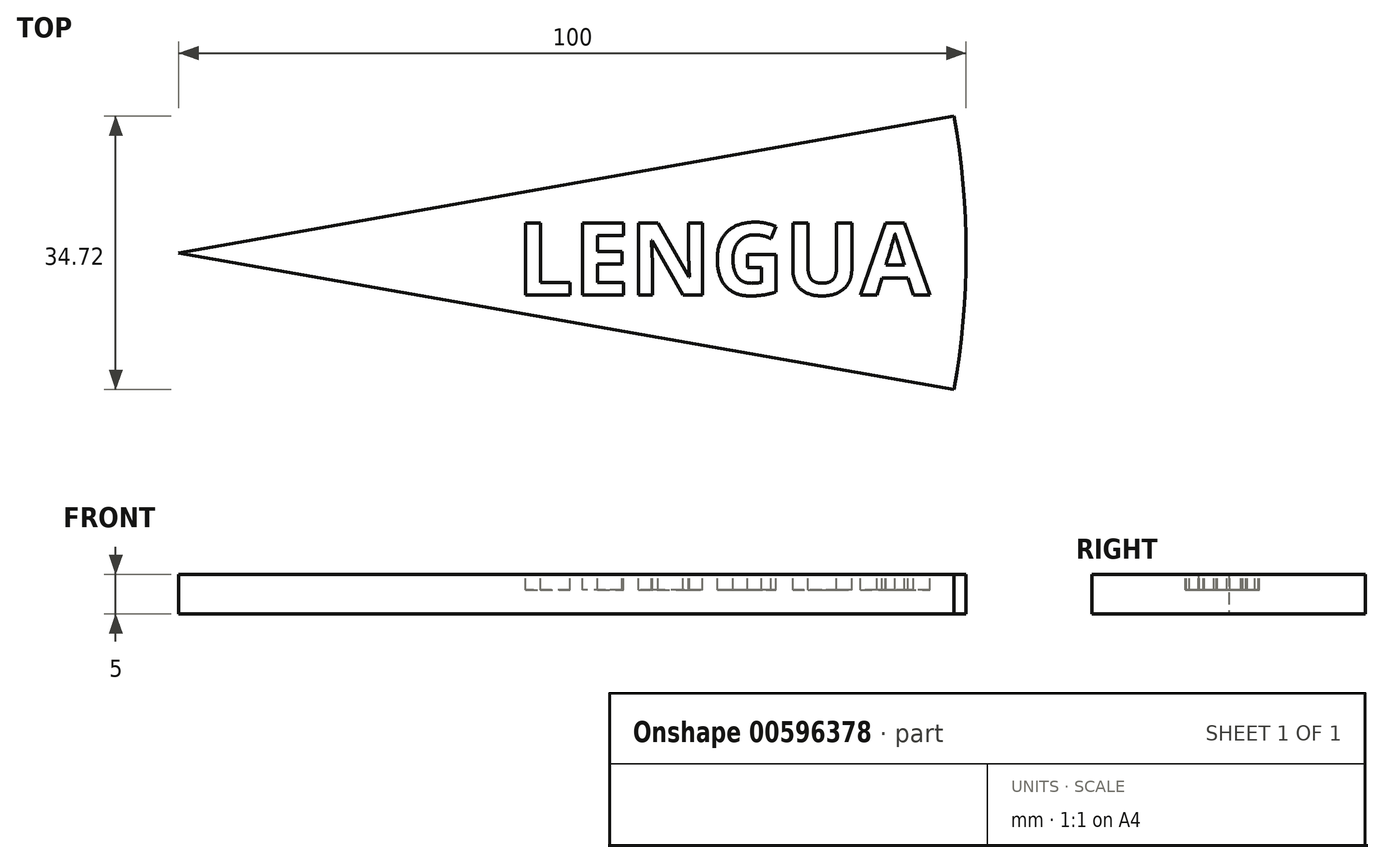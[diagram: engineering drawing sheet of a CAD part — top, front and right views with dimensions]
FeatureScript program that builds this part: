
annotation { "Feature Type Name" : "Feature", "Feature Type Description" : "" }
export const myFeature = defineFeature(function(context is Context, id is Id, definition is map)
    precondition{}
    {
        {
            var Q0;
            Q0=qCreatedBy(makeId("Top.planeOp"),FACE);
            var sketch = newSketch(context, id + "F0", { "sketchPlane" : qUnion([Q0])});
            skArc(sketch, "E0", {"start": v(98.48, -17.36) * mm, "mid": v(100, 0) * mm, "end": v(98.48, 17.36) * mm});
            skLineSegment(sketch, "E1", {"start": v(0, 0) * mm, "end": v(100, 0) * mm});
            skLineSegment(sketch, "E2", {"start": v(0, 0) * mm, "end": v(98.48, 17.36) * mm});
            skLineSegment(sketch, "E3", {"start": v(0, 0) * mm, "end": v(98.48, -17.36) * mm});
            skSolve(sketch);
        }
        {
            var Q0;
            Q0 = qSketchRegion(id + "F0", true);
            extrude(context, id + "F1", {"entities" : qUnion([Q0]), "depth" : 5 * mm, "offsetDistance" : 25 * mm});
        }
        {
            var Q0;
            Q0=makeQuery(id+"F1.opExtrude","CAP_FACE",FACE,{"disambiguationData":[OSD([sQuery(id+"F0.wireOp",EDGE,"E0"),sQuery(id+"F0.wireOp",EDGE,"E2"),sQuery(id+"F0.wireOp",EDGE,"E3")])],"isStart":false});
            var sketch = newSketch(context, id + "F2", { "sketchPlane" : qUnion([Q0])});
            skText(sketch, "E4", { "text": "LENGUA", "fontName": "OpenSans-Bold.ttf"});
            const initialGuessF2  = {"E4": [0.04289, -0.00536, 1, 0, 0.0092]};
            skSetInitialGuess(sketch, initialGuessF2);
            skSolve(sketch);
        }
        {
            var Q0;
            Q0 = qSketchRegion(id + "F2", true);
            extrude(context, id + "F3", {"entities" : qUnion([Q0]), "operationType" : NewBodyOperationType.REMOVE, "oppositeDirection" : true, "depth" : 2 * mm, "offsetDistance" : 25 * mm});
        }
    });
